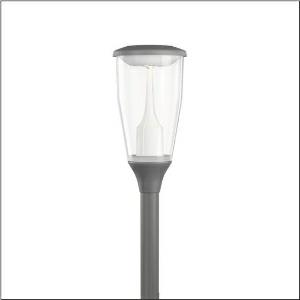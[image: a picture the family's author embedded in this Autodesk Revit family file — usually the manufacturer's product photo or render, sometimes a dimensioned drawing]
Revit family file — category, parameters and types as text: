
# Revit family: dl_11_iq___p1_0a_5xa5565ff14h000022_0ce9
name_source: partatom
category: Lighting Fixtures
units: mm (PartAtom-declared; Revit-internal decimal feet)

## family parameters
Cut with Voids When Loaded = No
Host = Face
Light Source = No
Part Type = Normal
Room Calculation Point = No
Round Connector Dimension = Use Diameter
Shared = No

## types (1)
- --- (1 x LED, 1530 lm, 10.5 W, 3000K)
    Apparent Load = 11 VA
    CIE Flux Codes = 34 63 91 95 100
    Color Rendering = 70
    Color Temperature = 3000K
    Default Elevation = 1800 mm
    Description = DL 11 iQ, mast luminaire, Module 540 iQ-SR, primary light control with 3 zone facetted reflector, of plastic, silver coated, highly specular, structured, primary optical cover: cover, of PMMA, transparent, light distribution: P1.0a, light emission: direct distribution, primary light characteristic: asymmetric, installation type: post-top, LED, High Power LED, rated luminous flux: 1.560lm, luminous efficacy: 149lm/W, light colour: 730, colour temperature: 3000K, control gear: iQ Street-Remote, control: Street-Remote, Auto-Match, Temp-Guard, Lumen-Switch, Night-Set, Smart-Wire, Light-Fading, Desk-Remote (wireless, voltage-free reading and setting of iQ features in the workshop via application-optimized NFC function/RFID function), optimised constant luminous flux control (CLO 2.0), mains connection: 220..240V, AC, 50/60Hz, connection cable pre-assembled, cable length: 5,5m, start of lifetime: 10W, end of service life: 11W, reduction: 5W, luminaire housing, upper part, of diecast aluminium, coated, SITECO metallic grey (DB 702S), spigot size: 60mm (post-top), mounting height: 3..5m, post-top mast mounting element, of diecast aluminium, coated, SITECO metallic grey (DB 702S), Module 540 iQ-SR, traffic white (RAL 9016), equipment: standard, protection rating (complete): IP66, insulation class (complete): insulation class II (safety insulation), certification: CE, ENEC, ENEC+, VDE, impact resistance: IK07, packaging unit: 1 piece

Light Distribution: P1.0a
    Height = 665 mm
    Lamp = 1 x LED
    Lamp Light Flux = 1530 lm
    Lamp Power = 10.5 W
    Lamp count = 1
    Length = 334 mm
    Luminous efficacy = 146 lm/W
    Manufacturer = Siteco
    ModVariant = No
    Model = 5XA5565FF14H000022
    Number of Poles = 1
    OnlyDefault = Yes
    Power Factor = 1
    Product Name = DL 11 iQ | P1.0a
    Product group = mast luminaire | pylon top
    ProductGroupID = 6100
    Protection Class = Protection class II
    Protection Degree = IP 66
    RLX_Detail_Level = 1
    RLX_Emergency_Light_Flux = 0 lm
    RLX_Emergency_Type = 0
    RLX_Emergency_Type_DB = No
    RlxData = <blob elided: 103397 chars, md5=83837e36>
    Socket = socket
    Standby Power = 0 W
    System Light Flux = 1530 lm
    System Power = 11 W
    Type Comments = factory setting: luminous flux: 100 % | dim-lin: 254 | 419 mA
    Type Image = l_1258354.jpg
    URL = http://relux.com
    VarID = @adj_095745
    Voltage = 0 V
    Weight = 0.00 kg
    Width = 0 mm  [stored 0 ft]

note: [stored X ft] marks values corroborated as IEEE doubles in the binary element streams (Revit-internal decimal feet)

## geometry (parser evidence)
native form markers: Blend x4, Sweep x9
no freeform markers — native parametric forms only
